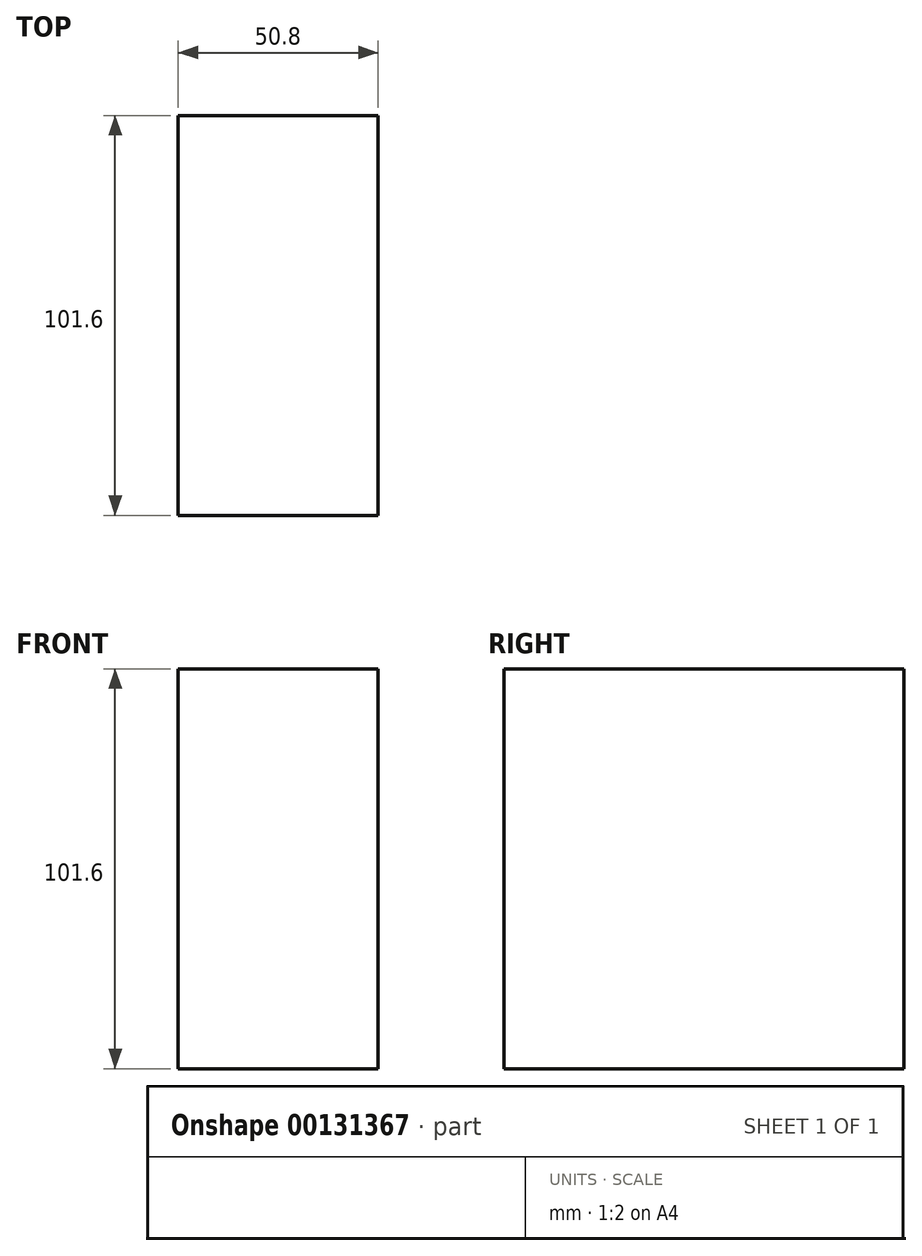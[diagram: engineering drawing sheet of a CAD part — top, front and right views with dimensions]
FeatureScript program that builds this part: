
annotation { "Feature Type Name" : "Feature", "Feature Type Description" : "" }
export const myFeature = defineFeature(function(context is Context, id is Id, definition is map)
    precondition{}
    {
        {
            var Q0;
            Q0=qCreatedBy(makeId("Front.planeOp"),FACE);
            var sketch = newSketch(context, id + "F0", { "sketchPlane" : qUnion([Q0])});
            skLineSegment(sketch, "E0.bottom", {"start": v(-25.4, 50.8) * mm, "end": v(25.4, 50.8) * mm});
            skLineSegment(sketch, "E0.top", {"start": v(-25.4, -50.8) * mm, "end": v(25.4, -50.8) * mm});
            skLineSegment(sketch, "E0.left", {"start": v(-25.4, 50.8) * mm, "end": v(-25.4, -50.8) * mm});
            skLineSegment(sketch, "E0.right", {"start": v(25.4, 50.8) * mm, "end": v(25.4, -50.8) * mm});
            skPoint(sketch, "E0.middle", {"position": v(0, 0) * mm});
            skSolve(sketch);
        }
        {
            var Q0;
            Q0 = qSketchRegion(id + "F0", true);
            extrude(context, id + "F1", {"entities" : qUnion([Q0]), "depth" : 101.6 * mm});
        }
    });
